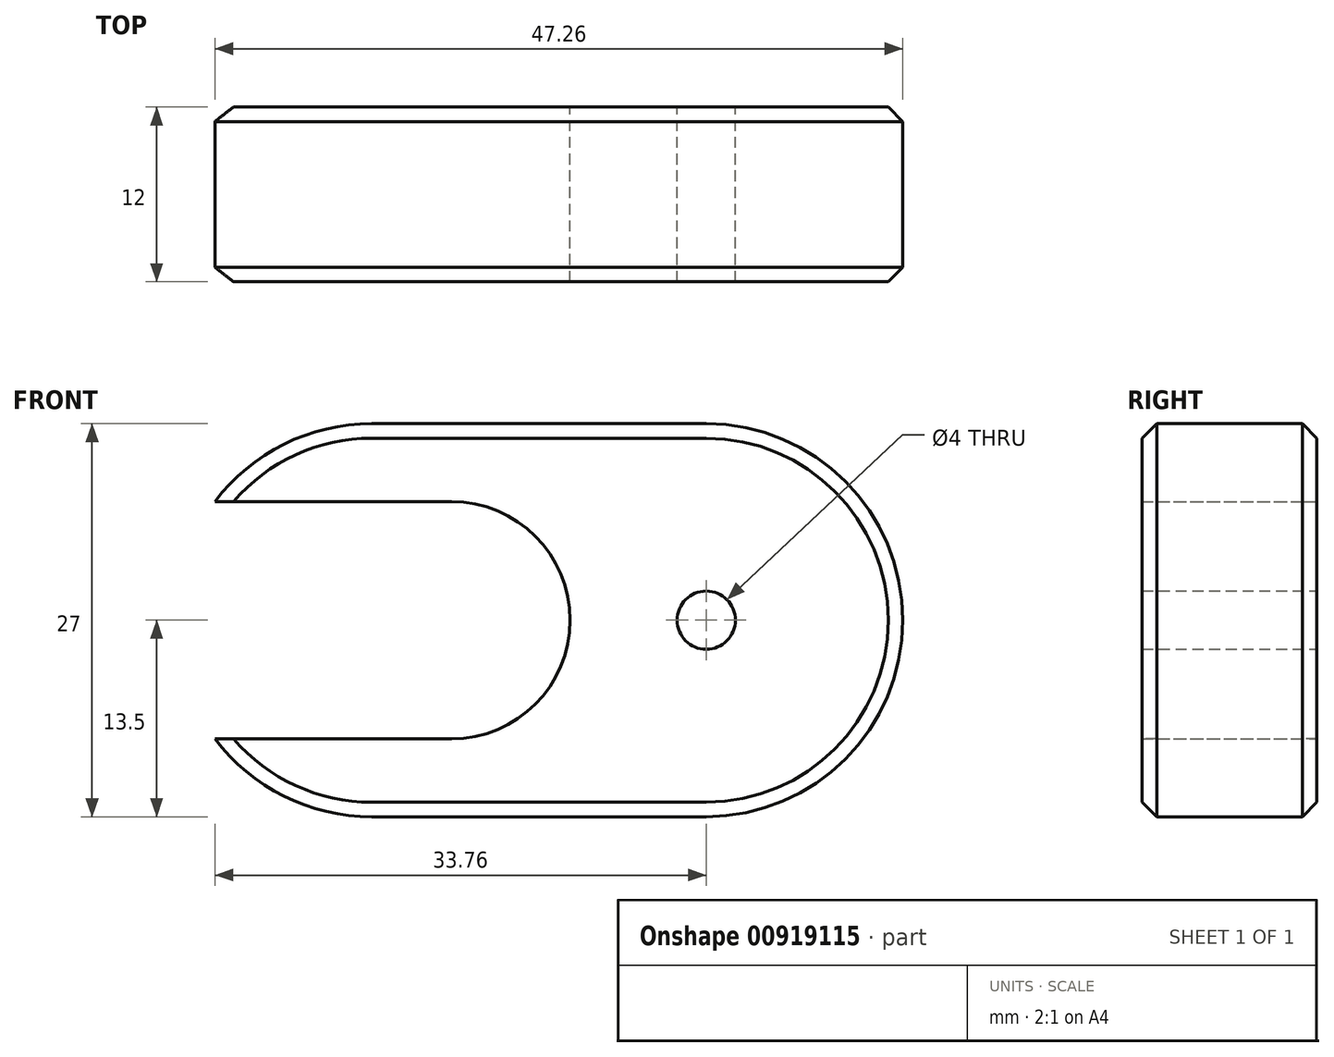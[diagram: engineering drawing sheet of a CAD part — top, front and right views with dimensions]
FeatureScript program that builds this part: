
annotation { "Feature Type Name" : "Feature", "Feature Type Description" : "" }
export const myFeature = defineFeature(function(context is Context, id is Id, definition is map)
    precondition{}
    {
        {
            var Q0;
            Q0=qCreatedBy(makeId("Front.planeOp"),FACE);
            var sketch = newSketch(context, id + "F0", { "sketchPlane" : qUnion([Q0])});
            skCircle(sketch, "E0", {"center": v(13.5, 0) * mm, "radius": 13.5 * mm});
            skCircle(sketch, "E1", {"center": v(-9.5, 0) * mm, "radius": 13.5 * mm});
            skLineSegment(sketch, "E2", {"start": v(-9.5, 13.5) * mm, "end": v(13.5, 13.5) * mm});
            skLineSegment(sketch, "E3", {"start": v(-9.5, -13.5) * mm, "end": v(13.5, -13.5) * mm});
            skLineSegment(sketch, "E4.bottom", {"start": v(-23, -8.15) * mm, "end": v(-4, -8.15) * mm});
            skLineSegment(sketch, "E4.top", {"start": v(-23, 8.15) * mm, "end": v(-4, 8.15) * mm});
            skLineSegment(sketch, "E4.left", {"start": v(-23, -8.15) * mm, "end": v(-23, 8.15) * mm});
            skLineSegment(sketch, "E4.right", {"start": v(-4, -8.15) * mm, "end": v(-4, 8.15) * mm});
            skPoint(sketch, "E4.middle", {"position": v(-13.5, 0) * mm});
            skCircle(sketch, "E5", {"center": v(-4, 0) * mm, "radius": 8.15 * mm});
            skCircle(sketch, "E6", {"center": v(13.5, 0) * mm, "radius": 2 * mm});
            skSolve(sketch);
        }
        {
            var Q0;
            {var subQ2=sQuery(id+"F0.wireOp",EDGE,"E0");var subQ6=sQuery(id+"F0.wireOp",EDGE,"E5");var subQ8=makeQuery(id+"F0.imprint","INTERSECT",VERTEX,{"disambiguationData":[OD(1.0)],"derivedFrom":[subQ2,subQ6]});Q0=makeQuery(id+"F0.imprint","IMPRINT",FACE,{"disambiguationData":[TD([[makeQuery(id+"F0.imprint","IMPRINT",EDGE,{"disambiguationData":[TD([[subQ8,-1.0]])],"derivedFrom":subQ2}),-1.0]])]});}
            var Q1;
            {var subQ0=sQuery(id+"F0.wireOp",EDGE,"E3");Q1=makeQuery(id+"F0.imprint","IMPRINT",FACE,{"disambiguationData":[TD([[makeQuery(id+"F0.imprint","IMPRINT",EDGE,{"derivedFrom":subQ0}),1.0]])]});}
            var Q2;
            {var subQ3=sQuery(id+"F0.wireOp",EDGE,"E1");var subQ6=sQuery(id+"F0.wireOp",EDGE,"E0");var subQ7=makeQuery(id+"F0.imprint","INTERSECT",VERTEX,{"disambiguationData":[OD(0.0)],"derivedFrom":[subQ6,subQ3]});Q2=makeQuery(id+"F0.imprint","IMPRINT",FACE,{"disambiguationData":[TD([[makeQuery(id+"F0.imprint","IMPRINT",EDGE,{"disambiguationData":[TD([[subQ7,-1.0]])],"derivedFrom":subQ6}),-1.0]])]});}
            var Q3;
            {var subQ0=sQuery(id+"F0.wireOp",EDGE,"E1");var subQ1=sQuery(id+"F0.wireOp",EDGE,"E0");var subQ2=makeQuery(id+"F0.imprint","INTERSECT",VERTEX,{"disambiguationData":[OD(0.0)],"derivedFrom":[subQ1,subQ0]});Q3=makeQuery(id+"F0.imprint","IMPRINT",FACE,{"disambiguationData":[TD([[makeQuery(id+"F0.imprint","IMPRINT",EDGE,{"disambiguationData":[TD([[subQ2,-1.0]])],"derivedFrom":subQ1}),1.0]])]});}
            var Q4;
            {var subQ0=sQuery(id+"F0.wireOp",EDGE,"E2");Q4=makeQuery(id+"F0.imprint","IMPRINT",FACE,{"disambiguationData":[TD([[makeQuery(id+"F0.imprint","IMPRINT",EDGE,{"derivedFrom":subQ0}),-1.0]])]});}
            var Q5;
            {var subQ1=sQuery(id+"F0.wireOp",EDGE,"E0");var subQ7=makeQuery(id+"F0.imprint","INTERSECT",VERTEX,{"derivedFrom":[subQ1,sQuery(id+"F0.wireOp",EDGE,"E2")]});Q5=makeQuery(id+"F0.imprint","IMPRINT",FACE,{"disambiguationData":[TD([[makeQuery(id+"F0.imprint","IMPRINT",EDGE,{"disambiguationData":[TD([[subQ7,-1.0]])],"derivedFrom":subQ1}),1.0]])]});}
            var Q6;
            {var subQ0=sQuery(id+"F0.wireOp",EDGE,"E5");var subQ1=sQuery(id+"F0.wireOp",EDGE,"E0");var subQ2=makeQuery(id+"F0.imprint","INTERSECT",VERTEX,{"disambiguationData":[OD(1.0)],"derivedFrom":[subQ1,subQ0]});Q6=makeQuery(id+"F0.imprint","IMPRINT",FACE,{"disambiguationData":[TD([[makeQuery(id+"F0.imprint","IMPRINT",EDGE,{"disambiguationData":[TD([[subQ2,-1.0]])],"derivedFrom":subQ1}),1.0]])]});}
            extrude(context, id + "F1", {"entities" : qUnion([Q0, Q1, Q2, Q3, Q4, Q5, Q6]), "depth" : 12 * mm, "offsetDistance" : 25 * mm});
        }
        {
            var Q0;
            Q0=makeQuery(id+"F1.opExtrude","CAP_EDGE",EDGE,{"disambiguationData":[OSD([sQuery(id+"F0.wireOp",EDGE,"E0")])],"isStart":false});
            var Q1;
            Q1=makeQuery(id+"F1.opExtrude","CAP_EDGE",EDGE,{"disambiguationData":[OSD([sQuery(id+"F0.wireOp",EDGE,"E0")])],"isStart":true});
            chamfer(context, id + "F2", {"entities" : qUnion([Q0, Q1]), "width" : 1 * mm, "tangentPropagation" : true});
        }
    });
